# Revit family: 141012027113804
name_source: partatom
category: Modelos genéricos
revit_build: Autodesk Revit 2018 (Build: 20190510_1515(x64)
units: mm (PartAtom-declared; Revit-internal decimal feet)

## family parameters
Compartido = No
Corte con vacíos al cargar = No
Cota de conector redondo = Diámetro de uso
Puede alojar armadura = No
Punto de cálculo de habitación = No
Se basa en plano de trabajo = No
Siempre vertical = No
Tipo de pieza = Normal

## types (1)
- PISO ESTOPEROL GOMA 1MTX3MM NEGRO ROLLO 20MT
    Alto = 3 mm  [stored 0.00984252 ft]
    Aplicacion = Donde se requiera una solucion antideslizante en solados.
    Color = Negro
    Descripción = Piso Estoperol antideslizante
    Dimension = 1000 mm  [stored 3.28084 ft]
    Empresa = CNP SPA.
    Espesor = 3 mm  [stored 0.00984252 ft]
    Largo = 1000 mm  [stored 3.28084 ft]
    Material = Goma negro
    Modelo = PISO ESTOPEROL GOMA
    Nombre SKU = PISO ESTOPEROL GOMA 1MTX3MM NEGRO ROLLO 20MT
    Num SKUs = 141012027113804
    URL = https://www.empresascnp.cl
    Unidad = Rollo 20m.
    Url Ficha tecnica = https://empresascnp.cl
    Uso = Es un producto que se puede instala en los descansos de las escaleras o tambien en
pisos de medio o alto tráfico cómo pasillos de edificios, aeropuertos, entre otros. Es una
solución fabricada en caucho natural con diseños antideslizantes. Ideal para: Edificios Públicos y Privados, Colegios, Universidades, Centros comerciales, Aeropuertos, Hoteles,
Edificios Habitacionales, entre otros.

note: [stored X ft] marks values corroborated as IEEE doubles in the binary element streams (Revit-internal decimal feet)

## geometry (parser evidence)
native form markers: Sweep x2
no freeform markers — native parametric forms only
